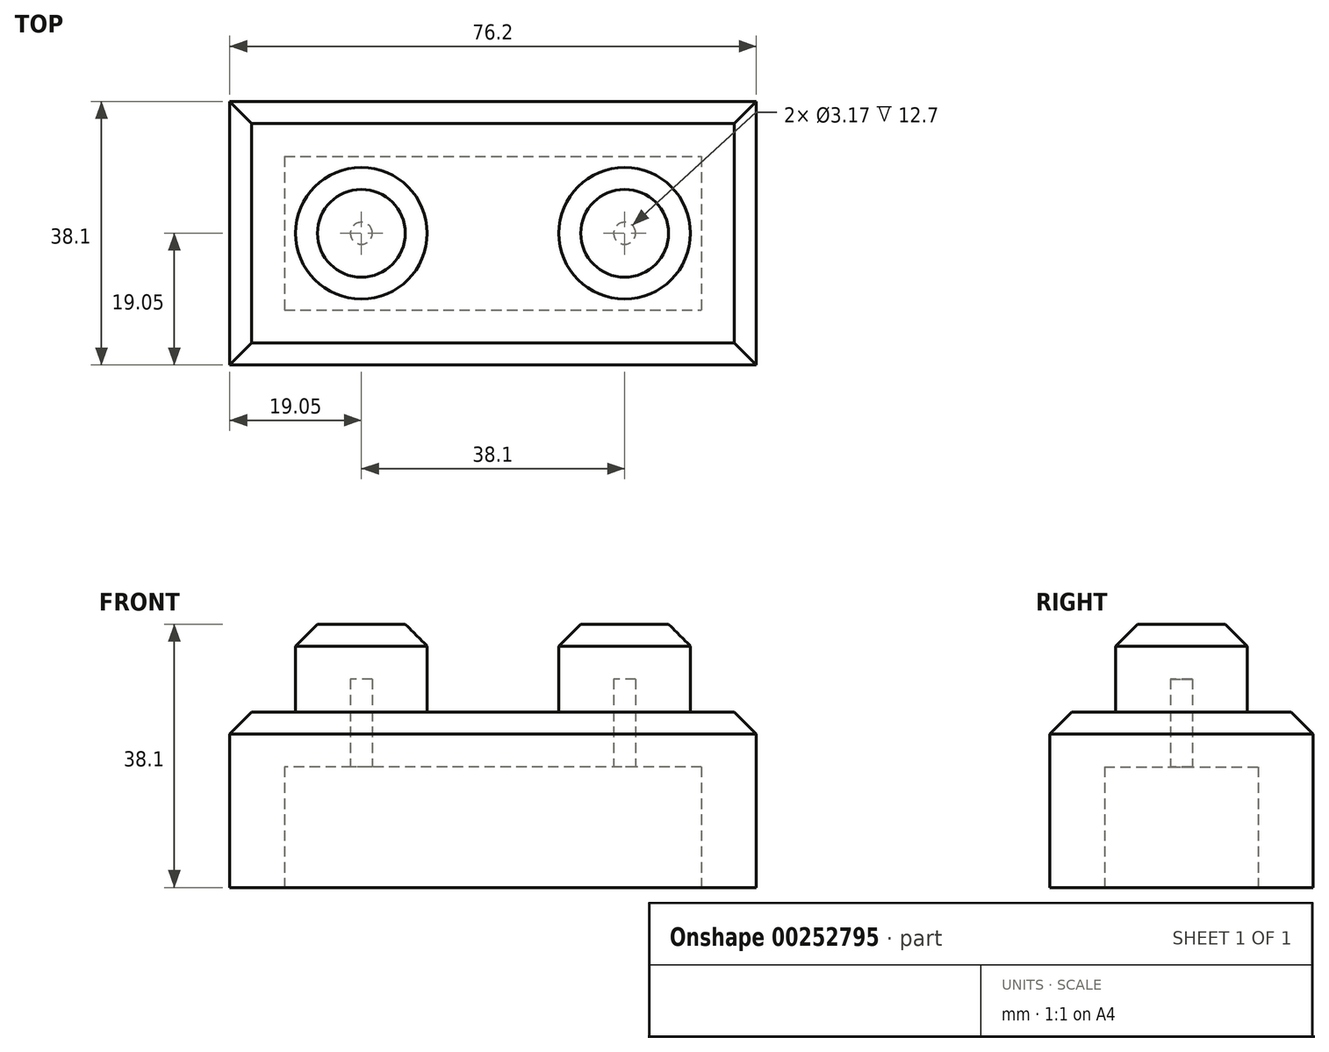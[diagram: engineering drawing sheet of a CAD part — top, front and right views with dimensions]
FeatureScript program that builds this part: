
annotation { "Feature Type Name" : "Feature", "Feature Type Description" : "" }
export const myFeature = defineFeature(function(context is Context, id is Id, definition is map)
    precondition{}
    {
        {
            var Q0;
            Q0=qCreatedBy(makeId("Top.planeOp"),FACE);
            var sketch = newSketch(context, id + "F0", { "sketchPlane" : qUnion([Q0])});
            skLineSegment(sketch, "E0.bottom", {"start": v(0, 0) * mm, "end": v(76.2, 0) * mm});
            skLineSegment(sketch, "E0.top", {"start": v(0, -38.1) * mm, "end": v(76.2, -38.1) * mm});
            skLineSegment(sketch, "E0.left", {"start": v(0, 0) * mm, "end": v(0, -38.1) * mm});
            skLineSegment(sketch, "E0.right", {"start": v(76.2, 0) * mm, "end": v(76.2, -38.1) * mm});
            skSolve(sketch);
        }
        {
            var Q0;
            Q0 = qSketchRegion(id + "F0", true);
            extrude(context, id + "F1", {"entities" : qUnion([Q0]), "depth" : 25.4 * mm});
        }
        {
            var Q0;
            Q0=makeQuery(id+"F1.opExtrude","CAP_FACE",FACE,{"disambiguationData":[OSD([sQuery(id+"F0.wireOp",EDGE,"E0.bottom"),sQuery(id+"F0.wireOp",EDGE,"E0.top"),sQuery(id+"F0.wireOp",EDGE,"E0.left"),sQuery(id+"F0.wireOp",EDGE,"E0.right")])],"isStart":false});
            var sketch = newSketch(context, id + "F2", { "sketchPlane" : qUnion([Q0])});
            skCircle(sketch, "E1", {"center": v(19.05, -19.05) * mm, "radius": 9.53 * mm});
            skCircle(sketch, "E2", {"center": v(57.15, -19.05) * mm, "radius": 9.53 * mm});
            skSolve(sketch);
        }
        {
            var Q0;
            Q0=makeQuery(id+"F2.imprint","IMPRINT",FACE,{"disambiguationData":[TD([[makeQuery(id+"F2.imprint","IMPRINT",EDGE,{"derivedFrom":sQuery(id+"F2.wireOp",EDGE,"E1")}),1.0]])]});
            var Q1;
            Q1=makeQuery(id+"F2.imprint","IMPRINT",FACE,{"disambiguationData":[TD([[makeQuery(id+"F2.imprint","IMPRINT",EDGE,{"derivedFrom":sQuery(id+"F2.wireOp",EDGE,"E2")}),1.0]])]});
            extrude(context, id + "F3", {"entities" : qUnion([Q0, Q1]), "operationType" : NewBodyOperationType.ADD, "depth" : 12.7 * mm});
        }
        {
            var Q0;
            Q0=makeQuery(id+"F3.opExtrude","CAP_EDGE",EDGE,{"disambiguationData":[OSD([sQuery(id+"F2.wireOp",EDGE,"E1")])],"isStart":false});
            var Q1;
            Q1=makeQuery(id+"F3.opExtrude","CAP_EDGE",EDGE,{"disambiguationData":[OSD([sQuery(id+"F2.wireOp",EDGE,"E2")])],"isStart":false});
            var Q2;
            Q2=makeQuery(id+"F1.opExtrude","CAP_EDGE",EDGE,{"disambiguationData":[OSD([sQuery(id+"F0.wireOp",EDGE,"E0.top")])],"isStart":false});
            var Q3;
            Q3=makeQuery(id+"F1.opExtrude","CAP_EDGE",EDGE,{"disambiguationData":[OSD([sQuery(id+"F0.wireOp",EDGE,"E0.right")])],"isStart":false});
            var Q4;
            Q4=makeQuery(id+"F1.opExtrude","CAP_EDGE",EDGE,{"disambiguationData":[OSD([sQuery(id+"F0.wireOp",EDGE,"E0.left")])],"isStart":false});
            var Q5;
            Q5=makeQuery(id+"F1.opExtrude","CAP_EDGE",EDGE,{"disambiguationData":[OSD([sQuery(id+"F0.wireOp",EDGE,"E0.bottom")])],"isStart":false});
            chamfer(context, id + "F4", {"entities" : qUnion([Q0, Q1, Q2, Q3, Q4, Q5]), "chamferType" : ChamferType.OFFSET_ANGLE, "width" : 3.17 * mm, "oppositeDirection" : false, "angle" : 45 * degree, "tangentPropagation" : true});
        }
        {
            var Q0;
            Q0=makeQuery(id+"F1.opExtrude","CAP_FACE",FACE,{"disambiguationData":[OSD([sQuery(id+"F0.wireOp",EDGE,"E0.bottom"),sQuery(id+"F0.wireOp",EDGE,"E0.top"),sQuery(id+"F0.wireOp",EDGE,"E0.left"),sQuery(id+"F0.wireOp",EDGE,"E0.right")])],"isStart":true});
            shell(context, id + "F5", {"entities" : qUnion([Q0]), "thickness" : 7.94 * mm});
        }
    });
